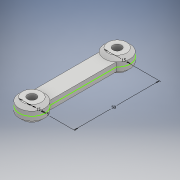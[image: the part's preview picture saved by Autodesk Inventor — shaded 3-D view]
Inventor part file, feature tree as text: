
AUTODESK INVENTOR PART (.ipt)
format: ipt  version: 2018 (Build 220112000, 112)  size: 129,536 bytes
history: native  units: mm
features: extrude x2, other x1, sketch x1, chamfer x1
ambient origin geometry x8: Origin, YZ Plane, XZ Plane, XY Plane, X Axis, Y Axis, Z Axis, Center Point
bodies: Body1 (feature_tree)
feature tree (5):
  other  "Твердое тело1"
  sketch  "Эскиз1"
  extrude  "Выдавливание1"  Depth=15.0mm
  extrude  "Выдавливание2"  Depth=15.0mm
  chamfer  "Фаска1"  Distance=5.0mm
